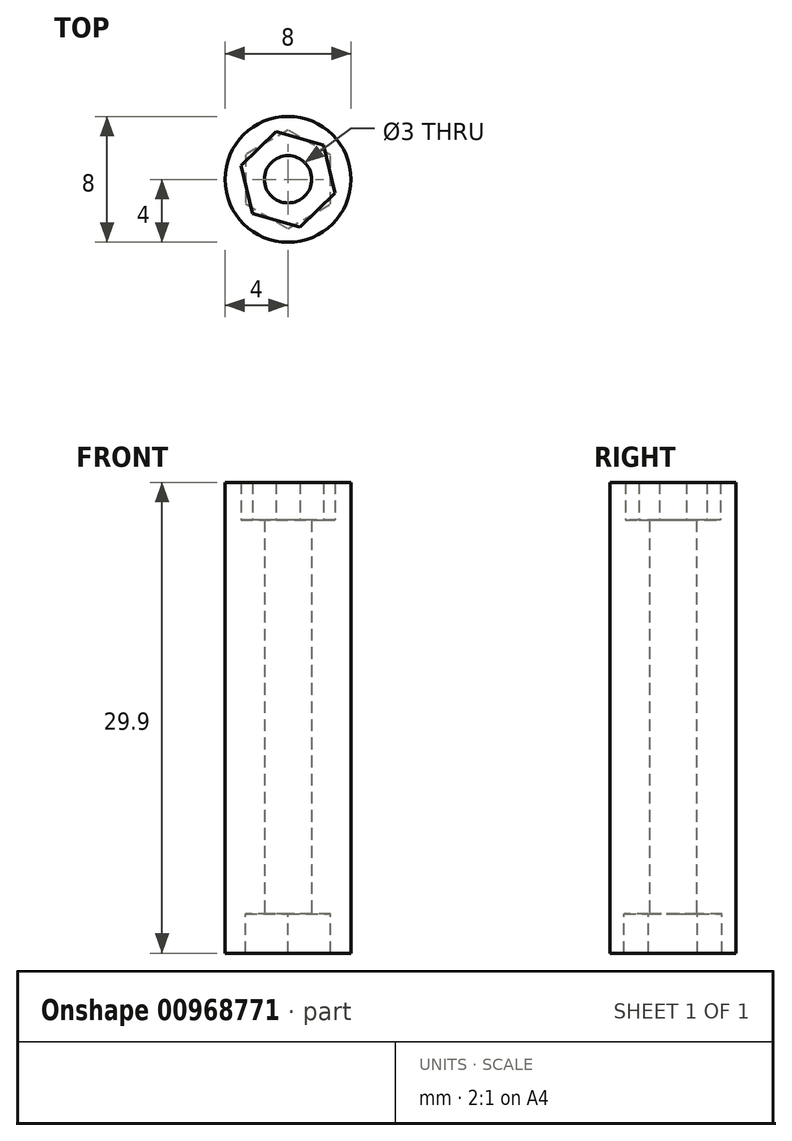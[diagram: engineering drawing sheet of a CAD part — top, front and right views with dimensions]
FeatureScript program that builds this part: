
annotation { "Feature Type Name" : "Feature", "Feature Type Description" : "" }
export const myFeature = defineFeature(function(context is Context, id is Id, definition is map)
    precondition{}
    {
        {
            var Q0;
            Q0=qCreatedBy(makeId("Top.planeOp"),FACE);
            var sketch = newSketch(context, id + "F0", { "sketchPlane" : qUnion([Q0])});
            skCircle(sketch, "E0", {"center": v(0, 0) * mm, "radius": 1.5 * mm});
            skCircle(sketch, "E1", {"center": v(0, 0) * mm, "radius": 4 * mm});
            skSolve(sketch);
        }
        {
            var Q0;
            Q0=makeQuery(id+"F0.imprint","IMPRINT",FACE,{"disambiguationData":[TD([[makeQuery(id+"F0.imprint","IMPRINT",EDGE,{"derivedFrom":sQuery(id+"F0.wireOp",EDGE,"E0")}),-1.0]])]});
            extrude(context, id + "F1", {"entities" : qUnion([Q0]), "flatOperationType" : FlatOperationType.REMOVE, "depth" : 25 * mm, "offsetDistance" : 25 * mm, "domain" : OperationDomain.MODEL});
        }
        {
            var Q0;
            Q0=makeQuery(id+"F1.opExtrude","CAP_FACE",FACE,{"disambiguationData":[OSD([sQuery(id+"F0.wireOp",EDGE,"E0"),sQuery(id+"F0.wireOp",EDGE,"E1")])],"isStart":false});
            var sketch = newSketch(context, id + "F2", { "sketchPlane" : qUnion([Q0])});
            skCircle(sketch, "E2.cCircle", {"center": v(0, 0) * mm, "radius": 2.7 * mm, "construction": true});
            skLineSegment(sketch, "E2.0", {"start": v(3, -0.86) * mm, "end": v(0.75, -3.03) * mm});
            skLineSegment(sketch, "E2.1", {"start": v(0.75, -3.03) * mm, "end": v(-2.24, -2.16) * mm});
            skLineSegment(sketch, "E2.2", {"start": v(-2.24, -2.16) * mm, "end": v(-3, 0.86) * mm});
            skLineSegment(sketch, "E2.3", {"start": v(-3, 0.86) * mm, "end": v(-0.75, 3.03) * mm});
            skLineSegment(sketch, "E2.4", {"start": v(-0.75, 3.03) * mm, "end": v(2.24, 2.16) * mm});
            skLineSegment(sketch, "E2.5", {"start": v(2.24, 2.16) * mm, "end": v(3, -0.86) * mm});
            skPoint(sketch, "E2.0.midPoint", {"position": v(1.87, -1.94) * mm});
            skSolve(sketch);
        }
        {
            var Q0;
            Q0=makeQuery(id+"F2.imprint","IMPRINT",FACE,{"disambiguationData":[TD([[makeQuery(id+"F2.imprint","IMPRINT",EDGE,{"derivedFrom":sQuery(id+"F2.wireOp",EDGE,"E2.0")}),1.0]])]});
            extrude(context, id + "F3", {"entities" : qUnion([Q0]), "operationType" : NewBodyOperationType.ADD, "flatOperationType" : FlatOperationType.REMOVE, "depth" : 2.4 * mm, "offsetDistance" : 25 * mm, "domain" : OperationDomain.MODEL});
        }
        {
            var Q0;
            Q0=makeQuery(id+"F1.opExtrude","CAP_FACE",FACE,{"disambiguationData":[OSD([sQuery(id+"F0.wireOp",EDGE,"E0"),sQuery(id+"F0.wireOp",EDGE,"E1")])],"isStart":true});
            var sketch = newSketch(context, id + "F4", { "sketchPlane" : qUnion([Q0])});
            skCircle(sketch, "E3.cCircle", {"center": v(0, 0) * mm, "radius": 2.7 * mm, "construction": true});
            skLineSegment(sketch, "E3.0", {"start": v(2.7, -1.55) * mm, "end": v(0, -3.12) * mm});
            skLineSegment(sketch, "E3.1", {"start": v(0, -3.12) * mm, "end": v(-2.7, -1.57) * mm});
            skLineSegment(sketch, "E3.2", {"start": v(-2.7, -1.57) * mm, "end": v(-2.7, 1.55) * mm});
            skLineSegment(sketch, "E3.3", {"start": v(-2.7, 1.55) * mm, "end": v(0, 3.12) * mm});
            skLineSegment(sketch, "E3.4", {"start": v(0, 3.12) * mm, "end": v(2.7, 1.57) * mm});
            skLineSegment(sketch, "E3.5", {"start": v(2.7, 1.57) * mm, "end": v(2.7, -1.55) * mm});
            skPoint(sketch, "E3.0.midPoint", {"position": v(1.36, -2.33) * mm});
            skSolve(sketch);
        }
        {
            var Q0;
            Q0=makeQuery(id+"F4.imprint","IMPRINT",FACE,{"disambiguationData":[TD([[makeQuery(id+"F4.imprint","IMPRINT",EDGE,{"derivedFrom":sQuery(id+"F4.wireOp",EDGE,"E3.0")}),1.0]])]});
            extrude(context, id + "F5", {"entities" : qUnion([Q0]), "operationType" : NewBodyOperationType.ADD, "depth" : 2.5 * mm, "offsetDistance" : 25 * mm});
        }
    });
